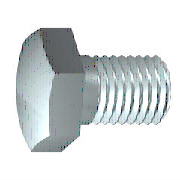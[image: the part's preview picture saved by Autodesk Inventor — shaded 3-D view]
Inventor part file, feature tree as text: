
AUTODESK INVENTOR PART (.ipt)
format: ipt  version: 2013 (Build 170138000, 138)  size: 185,344 bytes
history: native  units: mm (DEFAULTED — no unit token found)
features: sketch x2, extrude x1, chamfer x1, plane x1
ambient origin geometry x7: Origin, YZ Plane, XZ Plane, X Axis, Y Axis, Z Axis, Center Point
bodies: Solid1 (feature_tree), Body (feature_tree)
feature tree (5):
  extrude  "Head"  TaperAngle=90.0deg  [1 undecoded]
  chamfer  "Chamfer1"  [1 undecoded]
  plane  "Work Plane1"
  sketch  "Sketch1"  dims[d2=8.0mm d12=90.0deg]
  sketch  "Sketch2"  dims[d3=5.68mm d4=0.0mm d21=90.0deg d6=0.766813mm d7=0.766912mm d8=0.0mm d11=13.0mm d15=22.0mm d16=0.0mm d55=45.0deg d58=0.0mm d59=55.0mm d65=13.0mm d67=30.0deg d68=15.6mm d69=5.68mm d71=0.1mm d73=0.0mm]
note: 2 required parameter values undecoded (feature->parameter linkage not recoverable at this tier; creation-order binding heuristic only, values carry confidence <= 0.55)
